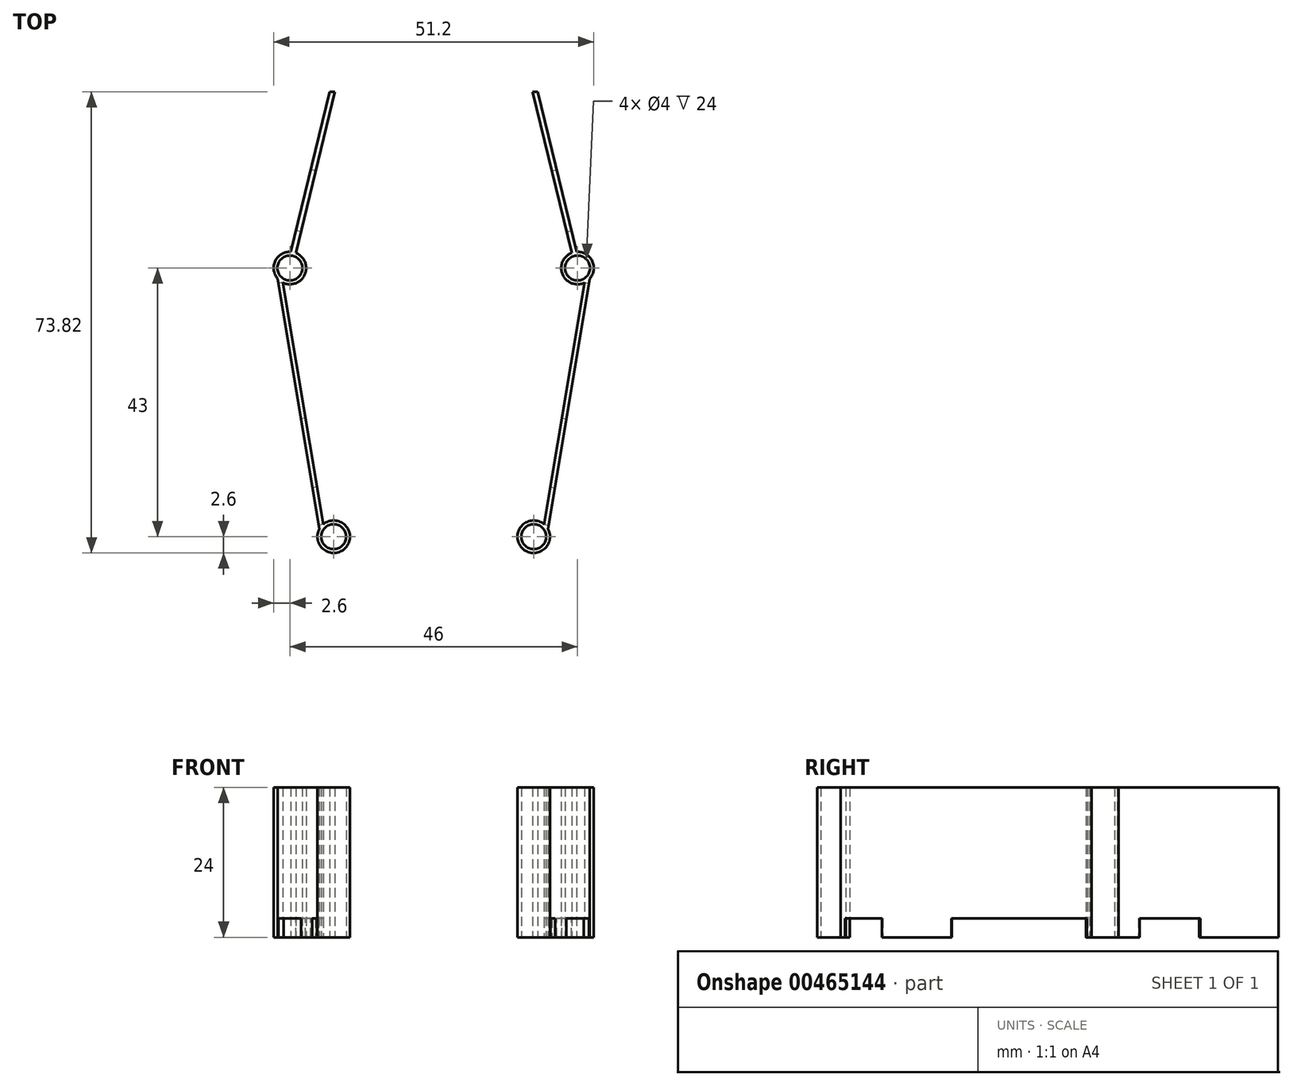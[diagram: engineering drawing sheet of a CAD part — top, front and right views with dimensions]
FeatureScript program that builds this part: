
annotation { "Feature Type Name" : "Feature", "Feature Type Description" : "" }
export const myFeature = defineFeature(function(context is Context, id is Id, definition is map)
    precondition{}
    {
        {
            var Q0;
            Q0=qCreatedBy(makeId("Top.planeOp"),FACE);
            var sketch = newSketch(context, id + "F0", { "sketchPlane" : qUnion([Q0])});
            skCircle(sketch, "E0", {"center": v(-23, 43) * mm, "radius": 2.6 * mm});
            skCircle(sketch, "E1", {"center": v(-16, 0) * mm, "radius": 2.6 * mm});
            skSolve(sketch);
        }
        {
            var Q0;
            Q0 = qSketchRegion(id + "F0", true);
            extrude(context, id + "F1", {"entities" : qUnion([Q0]), "depth" : 24 * mm});
        }
        {
            var Q0;
            Q0=qCreatedBy(makeId("Top.planeOp"),FACE);
            var sketch = newSketch(context, id + "F2", { "sketchPlane" : qUnion([Q0])});
            skCircle(sketch, "E2", {"center": v(-13, 85.6) * mm, "radius": 3.12 * mm});
            skSolve(sketch);
        }
        {
            var Q0;
            Q0=qCreatedBy(makeId("Top.planeOp"),FACE);
            var sketch = newSketch(context, id + "F3", { "sketchPlane" : qUnion([Q0])});
            skLineSegment(sketch, "E3", {"start": v(-25.3, 43.5) * mm, "end": v(-18.12, 0) * mm});
            skLineSegment(sketch, "E4", {"start": v(-18.12, 0) * mm, "end": v(-17.32, 0) * mm});
            skLineSegment(sketch, "E5", {"start": v(-17.32, 0) * mm, "end": v(-24.73, 44.05) * mm});
            skLineSegment(sketch, "E6", {"start": v(-25.3, 43.5) * mm, "end": v(-25.3, 43.5) * mm});
            skLineSegment(sketch, "E7", {"start": v(-25.3, 43.5) * mm, "end": v(-24.73, 44.05) * mm});
            skLineSegment(sketch, "E8", {"start": v(-23.3, 43.66) * mm, "end": v(-16.64, 71.22) * mm});
            skLineSegment(sketch, "E9", {"start": v(-15.84, 71.22) * mm, "end": v(-22.5, 43.61) * mm});
            skLineSegment(sketch, "E10", {"start": v(-16.64, 71.22) * mm, "end": v(-15.84, 71.22) * mm});
            skLineSegment(sketch, "E11", {"start": v(-23.3, 43.66) * mm, "end": v(-22.5, 43.61) * mm});
            skSolve(sketch);
        }
        {
            var Q0;
            Q0 = qSketchRegion(id + "F3", true);
            extrude(context, id + "F4", {"entities" : qUnion([Q0]), "operationType" : NewBodyOperationType.ADD, "depth" : 24 * mm});
        }
        {
            var Q0;
            Q0=sQuery(id+"F0.wireOp",VERTEX,"E0.center");
            var Q1;
            Q1=sQuery(id+"F0.wireOp",VERTEX,"E1.center");
            var Q2;
            Q2=makeQuery(id+"F1.opExtrude","SWEPT_BODY",BODY,{"disambiguationData":[OSD([sQuery(id+"F0.wireOp",EDGE,"E0")])]});
            hole(context, id + "F5", {"style" : HoleStyle.SIMPLE, "endStyle" : HoleEndStyle.THROUGH, "oppositeDirection" : true, "holeDiameter" : 4 * mm, "isTappedThrough" : true, "tappedDepth" : 12 * mm, "tapClearance" : 3, "locations" : qUnion([Q0, Q1]), "scope" : qUnion([Q2])});
        }
        {
            var Q0;
            Q0=makeQuery(id+"F4.opExtrude","SWEPT_FACE",FACE,{"disambiguationData":[OSD([sQuery(id+"F3.wireOp",EDGE,"E3")])]});
            var sketch = newSketch(context, id + "F6", { "sketchPlane" : qUnion([Q0])});
            skLineSegment(sketch, "E12", {"start": v(-44.07, 0) * mm, "end": v(-22.07, 0) * mm});
            skLineSegment(sketch, "E13", {"start": v(-22.07, 0) * mm, "end": v(-22.07, 3) * mm});
            skLineSegment(sketch, "E14", {"start": v(-44.07, 3) * mm, "end": v(-44.07, 0) * mm});
            skLineSegment(sketch, "E15.top", {"start": v(-4.86, 0) * mm, "end": v(-10.86, 0) * mm});
            skLineSegment(sketch, "E15.left", {"start": v(-4.86, 3) * mm, "end": v(-4.86, 0) * mm});
            skLineSegment(sketch, "E15.right", {"start": v(-10.86, 3) * mm, "end": v(-10.86, 0) * mm});
            skLineSegment(sketch, "E16", {"start": v(-44.07, 3) * mm, "end": v(-22.07, 3) * mm});
            skLineSegment(sketch, "E17", {"start": v(-10.86, 3) * mm, "end": v(-4.86, 3) * mm});
            skSolve(sketch);
        }
        {
            var Q0;
            Q0=makeQuery(id+"F6.imprint","IMPRINT",FACE,{"disambiguationData":[TD([[makeQuery(id+"F6.imprint","IMPRINT",EDGE,{"derivedFrom":sQuery(id+"F6.wireOp",EDGE,"E12")}),1.0]])]});
            var Q1;
            Q1=makeQuery(id+"F6.imprint","IMPRINT",FACE,{"disambiguationData":[TD([[makeQuery(id+"F6.imprint","IMPRINT",EDGE,{"derivedFrom":sQuery(id+"F6.wireOp",EDGE,"E15.top")}),1.0]])]});
            extrude(context, id + "F7", {"entities" : qUnion([Q0, Q1]), "operationType" : NewBodyOperationType.REMOVE, "oppositeDirection" : true, "depth" : 0.8 * mm});
        }
        {
            var Q0;
            Q0=makeQuery(id+"F4.opExtrude","SWEPT_FACE",FACE,{"disambiguationData":[OSD([sQuery(id+"F3.wireOp",EDGE,"E8")])]});
            var sketch = newSketch(context, id + "F8", { "sketchPlane" : qUnion([Q0])});
            skLineSegment(sketch, "E18.bottom", {"start": v(-52.45, 0) * mm, "end": v(-42.45, 0) * mm});
            skLineSegment(sketch, "E18.top", {"start": v(-52.45, 3) * mm, "end": v(-42.45, 3) * mm});
            skLineSegment(sketch, "E18.left", {"start": v(-52.45, 0) * mm, "end": v(-52.45, 3) * mm});
            skLineSegment(sketch, "E18.right", {"start": v(-42.45, 0) * mm, "end": v(-42.45, 3) * mm});
            skSolve(sketch);
        }
        {
            var Q0;
            Q0 = qSketchRegion(id + "F8", true);
            extrude(context, id + "F9", {"entities" : qUnion([Q0]), "operationType" : NewBodyOperationType.REMOVE, "oppositeDirection" : true, "depth" : 2 * mm});
        }
        {
            var Q0;
            Q0=makeQuery(id+"F1.opExtrude","SWEPT_BODY",BODY,{"disambiguationData":[OSD([sQuery(id+"F0.wireOp",EDGE,"E0")])]});
            var Q1;
            Q1=qCreatedBy(makeId("Right.planeOp"),FACE);
            mirror(context, id + "F10", {"entities" : qUnion([Q0]), "mirrorPlane" : qUnion([Q1])});
        }
    });
